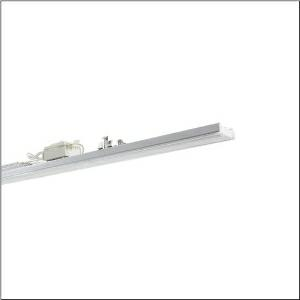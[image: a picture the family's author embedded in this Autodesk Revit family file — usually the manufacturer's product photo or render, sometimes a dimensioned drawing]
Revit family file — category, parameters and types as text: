
# Revit family: licross_r__21_recessed_ho_52tl11mn4fxs_9277
name_source: partatom
category: Lighting Fixtures
units: mm (PartAtom-declared; Revit-internal decimal feet)

## family parameters
Cut with Voids When Loaded = No
Host = Face
Light Source = No
Part Type = Normal
Room Calculation Point = No
Round Connector Dimension = Use Diameter
Shared = No

## types (1)
- --- (1 x LED, 15070 lm, 83.1 W, 4000K)
    Apparent Load = 83 VA
    CIE Flux Codes = 87 95 99 100 100
    Color Rendering = 80
    Color Temperature = 4000K
    Default Elevation = 1800 mm
    Description = Licross® 21 Recessed HO, luminaire insert, of sheet steel, galvanised, coil coated, white, length: 1.500mm, width: 66mm, height: 67mm, LED rated luminous flux: 15.060lm, light colour: 840, control gear: ON/OFF Multilumen, with plug, 3-pole, with phase selection, mains connection: 220..240V, AC, 50/60Hz, rated input power: 83W, halogen-free wiring, primary light control with lens, of plastic, primary optical cover: cover, of PMMA, light emission: direct distribution, primary light characteristic: symmetric, protection rating (complete): IP40, insulation class (complete): insulation class I (protective earthing), certification: CE, ENEC, VDE, UKCA, protection symbol: D if used in an environment without relevant dust loads with corresponding accessories, impact resistance: IK06, permissible ambient temperature for indoor applications: -35..+30°C, corresponds to IFS (International Featured Standards) requirements for safety and quality in the food industry, reducing of maximum allowable ambient temperature of 5°C with ceiling mounting, LABS conformity tested according to VDMA 24364:2018-05, packaging unit: 1 piece
    Height = 58 mm
    Lamp = 1 x LED
    Lamp Light Flux = 15070 lm
    Lamp Power = 83.1 W
    Lamp count = 1
    Length = 1500 mm
    Luminous efficacy = 181 lm/W
    Manufacturer = Siteco
    ModVariant = No
    Model = 52TL11MN4FXS
    Mounting Place = Ceiling
    Mounting Type = Pendant
    Number of Poles = 1
    OnlyDefault = Yes
    Power Factor = 1
    Product Name = Licross® 21 Recessed HO
    Product group = luminaire insert
    ProductGroupID = 902
    Protection Class = Protection class I
    Protection Degree = IP 40
    RLX_Detail_Level = 1
    RLX_Emergency_Light_Flux = 0 lm
    RLX_Emergency_Type = 0
    RLX_Emergency_Type_DB = No
    RlxData = <blob elided: 22221 chars, md5=7e7856a5>
    Socket = socket
    Standby Power = 0 W
    System Light Flux = 15070 lm
    System Power = 83 W
    Type Comments = factory setting: luminous flux: 100 % | (A | C | E) | 195 mA
    Type Image = l_1296930.jpg
    URL = http://relux.com
    VarID = @adj_108066
    Voltage = 0 V
    Weight = 0.00 kg
    Width = 66 mm

## geometry (parser evidence)
native form markers: Blend x4, Sweep x11
no freeform markers — native parametric forms only
